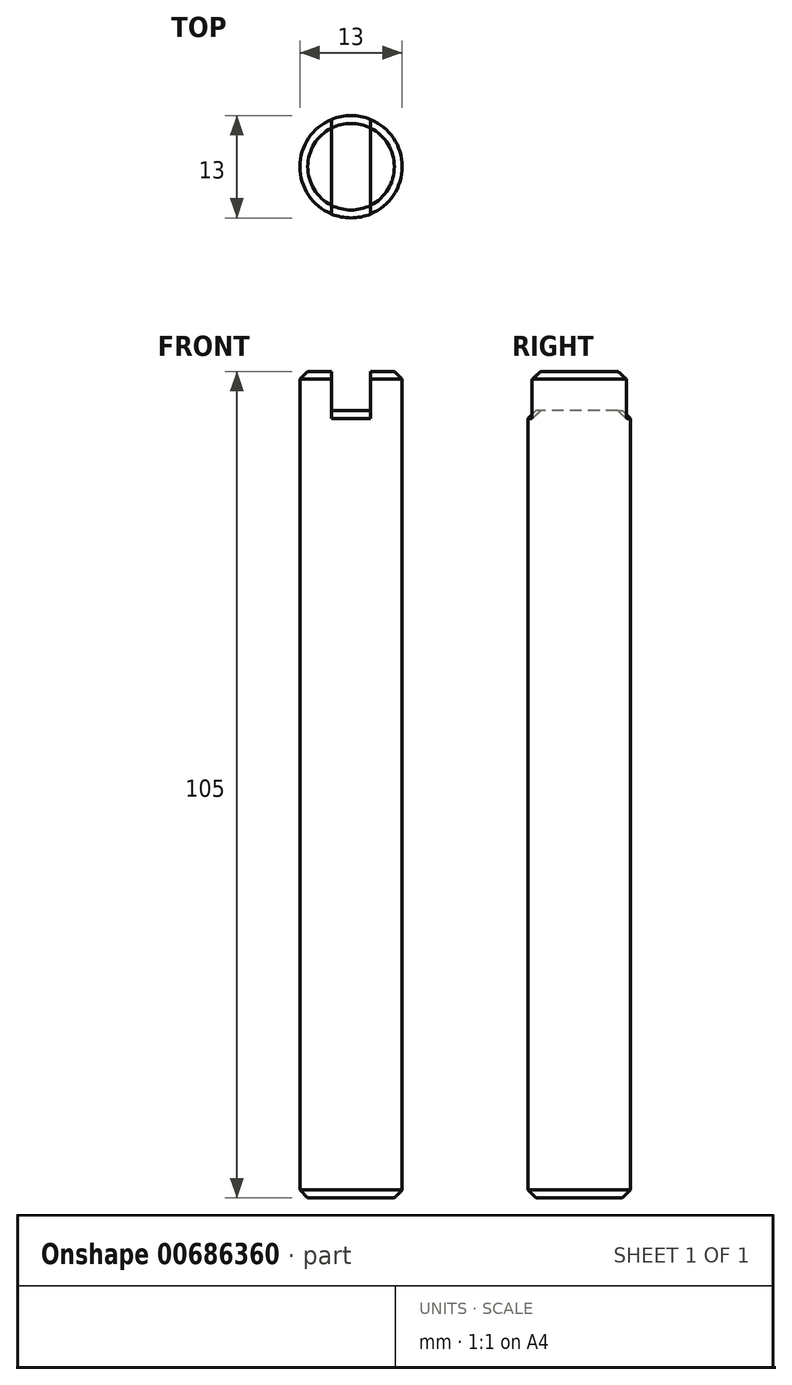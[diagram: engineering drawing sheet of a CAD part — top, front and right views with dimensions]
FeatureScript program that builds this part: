
annotation { "Feature Type Name" : "Feature", "Feature Type Description" : "" }
export const myFeature = defineFeature(function(context is Context, id is Id, definition is map)
    precondition{}
    {
        {
            var Q0;
            Q0=qCreatedBy(makeId("Top.planeOp"),FACE);
            var sketch = newSketch(context, id + "F0", { "sketchPlane" : qUnion([Q0])});
            skCircle(sketch, "E0", {"center": v(0, 0) * mm, "radius": 6.5 * mm});
            skLineSegment(sketch, "E1", {"start": v(0, 6.5) * mm, "end": v(0, -6.5) * mm, "construction": true});
            skLineSegment(sketch, "E2", {"start": v(-2.5, 6.5) * mm, "end": v(2.5, 6.5) * mm, "construction": true});
            skPoint(sketch, "E3", {"position": v(0, 6.5) * mm});
            skLineSegment(sketch, "E4", {"start": v(-2.5, 6) * mm, "end": v(-2.5, -6) * mm});
            skLineSegment(sketch, "E5", {"start": v(2.5, 6) * mm, "end": v(2.5, -6) * mm});
            skSolve(sketch);
        }
        {
            var Q0;
            {var subQ0=sQuery(id+"F0.wireOp",EDGE,"E4");Q0=makeQuery(id+"F0.imprint","IMPRINT",FACE,{"disambiguationData":[TD([[makeQuery(id+"F0.imprint","IMPRINT",EDGE,{"derivedFrom":subQ0}),-1.0]])]});}
            var Q1;
            {var subQ0=sQuery(id+"F0.wireOp",EDGE,"E5");Q1=makeQuery(id+"F0.imprint","IMPRINT",FACE,{"disambiguationData":[TD([[makeQuery(id+"F0.imprint","IMPRINT",EDGE,{"derivedFrom":subQ0}),1.0]])]});}
            var Q2;
            {var subQ0=sQuery(id+"F0.wireOp",EDGE,"E4");Q2=makeQuery(id+"F0.imprint","IMPRINT",FACE,{"disambiguationData":[TD([[makeQuery(id+"F0.imprint","IMPRINT",EDGE,{"derivedFrom":subQ0}),1.0]])]});}
            extrude(context, id + "F1", {"entities" : qUnion([Q0, Q1, Q2]), "oppositeDirection" : true, "depth" : 100 * mm, "offsetDistance" : 25 * mm});
        }
        {
            var Q0;
            {var subQ0=sQuery(id+"F0.wireOp",EDGE,"E4");Q0=makeQuery(id+"F0.imprint","IMPRINT",FACE,{"disambiguationData":[TD([[makeQuery(id+"F0.imprint","IMPRINT",EDGE,{"derivedFrom":subQ0}),-1.0]])]});}
            var Q1;
            {var subQ0=sQuery(id+"F0.wireOp",EDGE,"E5");Q1=makeQuery(id+"F0.imprint","IMPRINT",FACE,{"disambiguationData":[TD([[makeQuery(id+"F0.imprint","IMPRINT",EDGE,{"derivedFrom":subQ0}),1.0]])]});}
            extrude(context, id + "F2", {"entities" : qUnion([Q0, Q1]), "operationType" : NewBodyOperationType.ADD, "depth" : 5 * mm, "offsetDistance" : 25 * mm});
        }
        {
            var Q0;
            {var subQ0=sQuery(id+"F0.wireOp",EDGE,"E4");var subQ1=sQuery(id+"F0.wireOp",EDGE,"E0");Q0=makeQuery(id+"F2.opExtrude","CAP_EDGE",EDGE,{"disambiguationData":[OSD([subQ1]),TDD([makeQuery(id+"F0.imprint","IMPRINT",EDGE,{"disambiguationData":[TD([[makeQuery(id+"F0.imprint","INTERSECT",VERTEX,{"disambiguationData":[OD(0.0)],"derivedFrom":[subQ1,subQ0]}),-1.0]])],"derivedFrom":subQ1})])],"isStart":false});}
            var Q1;
            {var subQ0=sQuery(id+"F0.wireOp",EDGE,"E5");var subQ1=sQuery(id+"F0.wireOp",EDGE,"E0");Q1=makeQuery(id+"F2.opExtrude","CAP_EDGE",EDGE,{"disambiguationData":[OSD([subQ1]),TDD([makeQuery(id+"F0.imprint","IMPRINT",EDGE,{"disambiguationData":[TD([[makeQuery(id+"F0.imprint","INTERSECT",VERTEX,{"disambiguationData":[OD(0.0)],"derivedFrom":[subQ1,subQ0]}),1.0]])],"derivedFrom":subQ1})])],"isStart":false});}
            var Q2;
            Q2=makeQuery(id+"F1.opExtrude","CAP_EDGE",EDGE,{"disambiguationData":[OSD([sQuery(id+"F0.wireOp",EDGE,"E0")])],"isStart":false});
            var Q3;
            Q3=makeQuery(id+"F2.boolean.opBoolean","SPLIT",EDGE,{"disambiguationData":[OD(0.0)],"derivedFrom":makeQuery(id+"F1.opExtrude","CAP_EDGE",EDGE,{"disambiguationData":[OSD([sQuery(id+"F0.wireOp",EDGE,"E0")])],"isStart":true})});
            var Q4;
            Q4=makeQuery(id+"F2.boolean.opBoolean","SPLIT",EDGE,{"disambiguationData":[OD(1.0)],"derivedFrom":makeQuery(id+"F1.opExtrude","CAP_EDGE",EDGE,{"disambiguationData":[OSD([sQuery(id+"F0.wireOp",EDGE,"E0")])],"isStart":true})});
            chamfer(context, id + "F3", {"entities" : qUnion([Q0, Q1, Q2, Q3, Q4]), "width" : 1 * mm, "tangentPropagation" : true});
        }
    });
